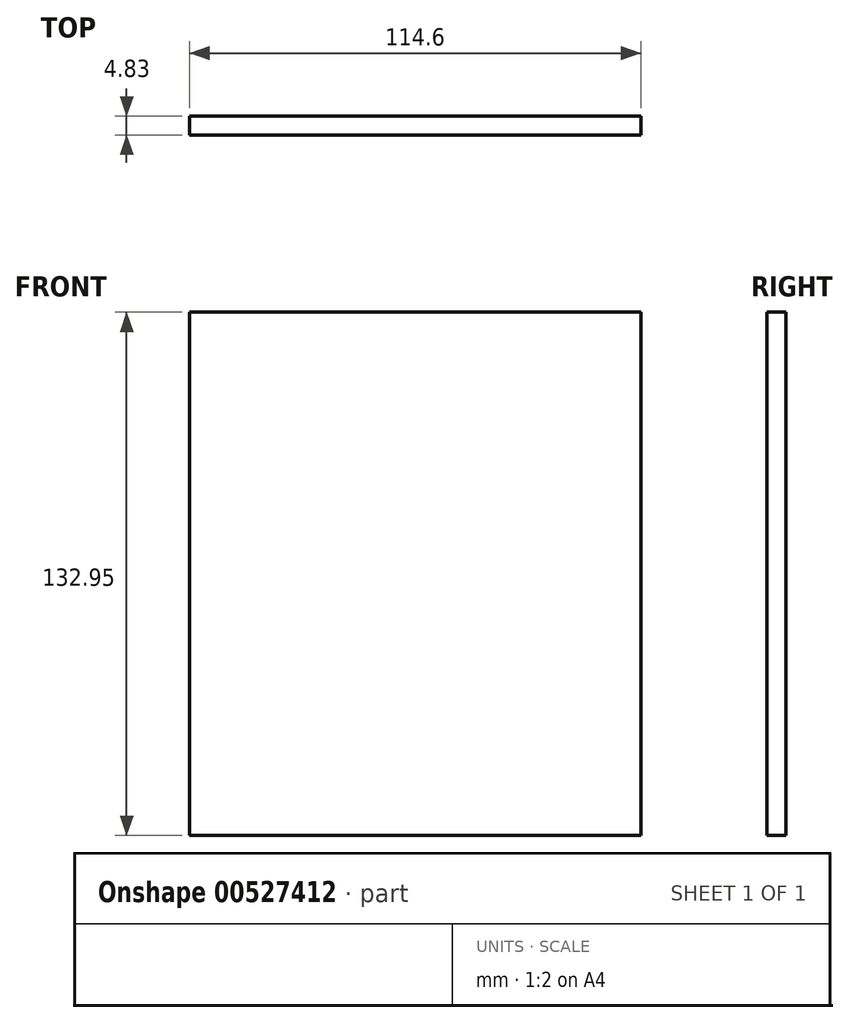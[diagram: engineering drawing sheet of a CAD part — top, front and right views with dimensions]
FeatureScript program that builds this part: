
annotation { "Feature Type Name" : "Feature", "Feature Type Description" : "" }
export const myFeature = defineFeature(function(context is Context, id is Id, definition is map)
    precondition{}
    {
        {
            var Q0;
            Q0=qCreatedBy(makeId("Front.planeOp"),FACE);
            var sketch = newSketch(context, id + "F0", { "sketchPlane" : qUnion([Q0])});
            skLineSegment(sketch, "E0.bottom", {"start": v(-56.55, 55.95) * mm, "end": v(58.05, 55.95) * mm});
            skLineSegment(sketch, "E0.top", {"start": v(-56.55, -77) * mm, "end": v(58.05, -77) * mm});
            skLineSegment(sketch, "E0.left", {"start": v(-56.55, 55.95) * mm, "end": v(-56.55, -77) * mm});
            skLineSegment(sketch, "E0.right", {"start": v(58.05, 55.95) * mm, "end": v(58.05, -77) * mm});
            skSolve(sketch);
        }
        {
            var Q0;
            Q0=makeQuery(id+"F0.imprint","IMPRINT",FACE,{"disambiguationData":[TD([[makeQuery(id+"F0.imprint","IMPRINT",EDGE,{"derivedFrom":sQuery(id+"F0.wireOp",EDGE,"E0.bottom")}),-1.0]])]});
            extrude(context, id + "F1", {"entities" : qUnion([Q0]), "depth" : 4.83 * mm, "offsetDistance" : 25.4 * mm});
        }
    });
